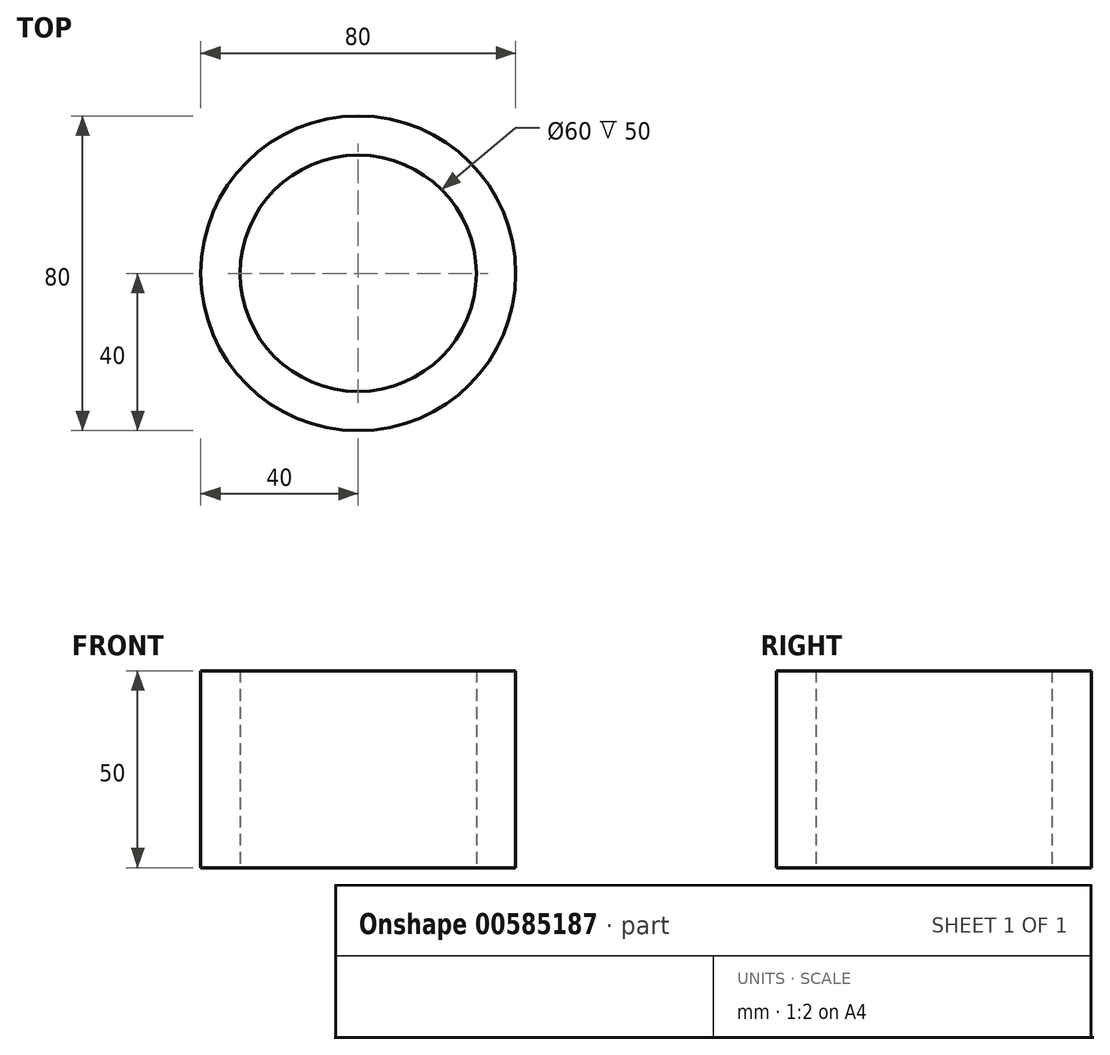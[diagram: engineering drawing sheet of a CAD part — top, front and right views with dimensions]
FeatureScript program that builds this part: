
annotation { "Feature Type Name" : "Feature", "Feature Type Description" : "" }
export const myFeature = defineFeature(function(context is Context, id is Id, definition is map)
    precondition{}
    {
        {
            var Q0;
            Q0=qCreatedBy(makeId("Top.planeOp"),FACE);
            var sketch = newSketch(context, id + "F0", { "sketchPlane" : qUnion([Q0])});
            skCircle(sketch, "E0", {"center": v(0, 0) * mm, "radius": 40 * mm});
            skCircle(sketch, "E1", {"center": v(0, 0) * mm, "radius": 30 * mm});
            skSolve(sketch);
        }
        {
            var Q0;
            Q0 = qSketchRegion(id + "F0", true);
            extrude(context, id + "F1", {"entities" : qUnion([Q0]), "depth" : 50 * mm, "offsetDistance" : 25 * mm});
        }
    });
